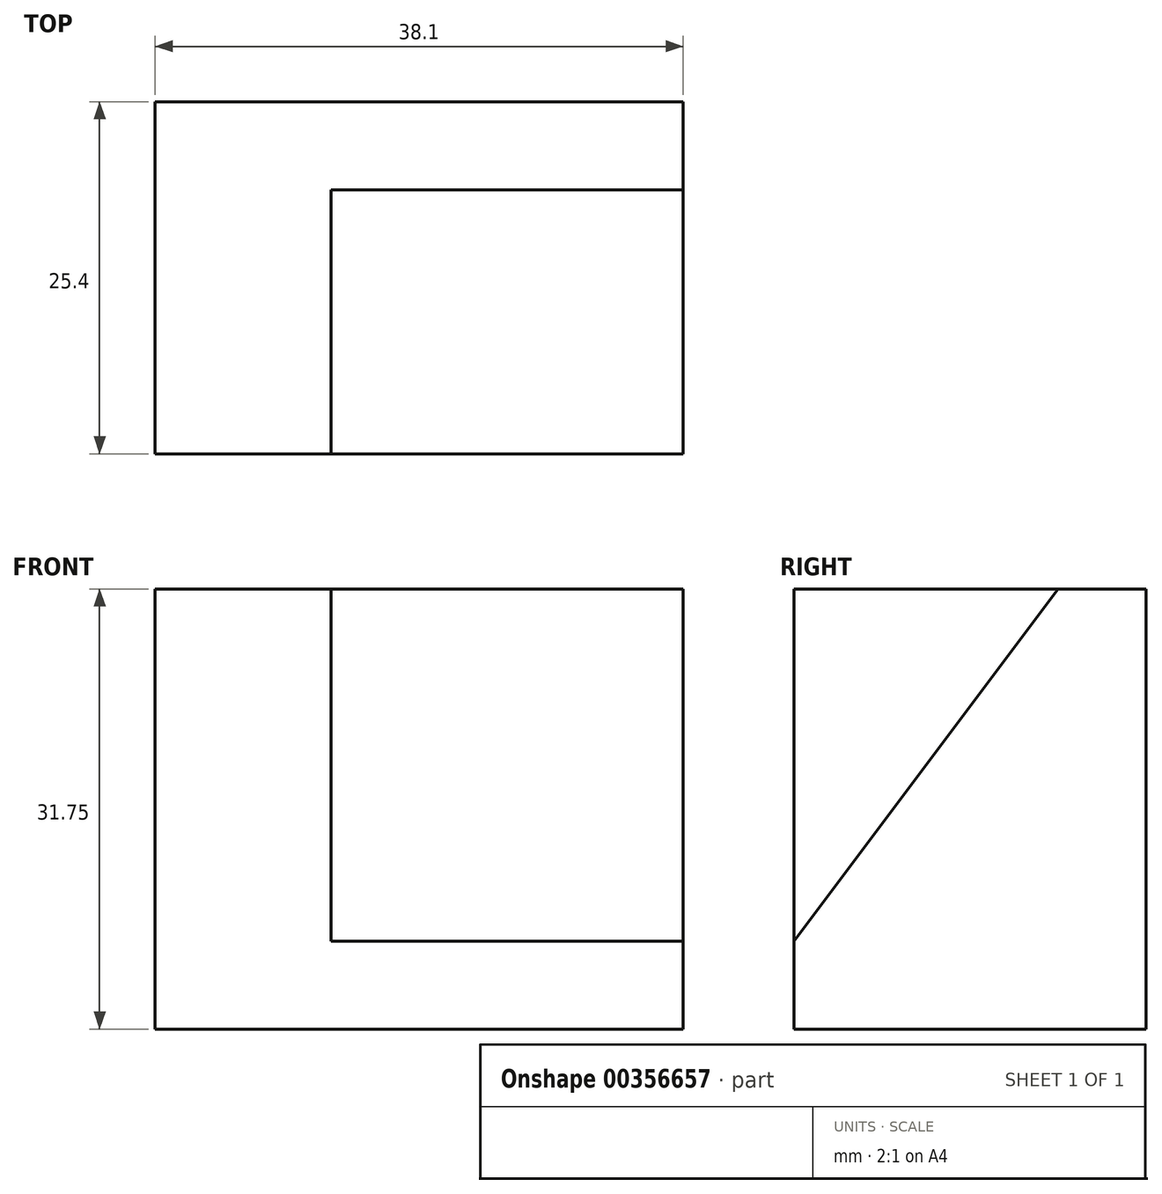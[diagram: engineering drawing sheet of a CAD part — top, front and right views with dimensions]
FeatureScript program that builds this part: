
annotation { "Feature Type Name" : "Feature", "Feature Type Description" : "" }
export const myFeature = defineFeature(function(context is Context, id is Id, definition is map)
    precondition{}
    {
        {
            var Q0;
            Q0=qCreatedBy(makeId("Front.planeOp"),FACE);
            var sketch = newSketch(context, id + "F0", { "sketchPlane" : qUnion([Q0])});
            skLineSegment(sketch, "E0", {"start": v(-35.9, 29.87) * mm, "end": v(-35.9, -1.88) * mm});
            skLineSegment(sketch, "E1", {"start": v(-35.9, -1.88) * mm, "end": v(2.2, -1.88) * mm});
            skLineSegment(sketch, "E2", {"start": v(2.2, -1.88) * mm, "end": v(2.2, 29.87) * mm});
            skLineSegment(sketch, "E3", {"start": v(2.2, 29.87) * mm, "end": v(-35.9, 29.87) * mm});
            skSolve(sketch);
        }
        {
            var Q0;
            Q0=makeQuery(id+"F0.imprint","IMPRINT",FACE,{"disambiguationData":[TD([[makeQuery(id+"F0.imprint","IMPRINT",EDGE,{"derivedFrom":sQuery(id+"F0.wireOp",EDGE,"E0")}),1.0]])]});
            extrude(context, id + "F1", {"entities" : qUnion([Q0]), "depth" : 25.4 * mm});
        }
        {
            var Q0;
            Q0=makeQuery(id+"F1.opExtrude","SWEPT_FACE",FACE,{"disambiguationData":[OSD([sQuery(id+"F0.wireOp",EDGE,"E3")])]});
            var sketch = newSketch(context, id + "F2", { "sketchPlane" : qUnion([Q0])});
            skLineSegment(sketch, "E4", {"start": v(2.2, -6.35) * mm, "end": v(-23.2, -6.35) * mm});
            skLineSegment(sketch, "E5", {"start": v(-23.2, -6.35) * mm, "end": v(-23.2, -25.4) * mm});
            skSolve(sketch);
        }
        {
            var Q0;
            {var subQ0=sQuery(id+"F2.wireOp",EDGE,"E4");Q0=makeQuery(id+"F2.imprint","IMPRINT",FACE,{"disambiguationData":[TD([[makeQuery(id+"F2.imprint","IMPRINT",EDGE,{"derivedFrom":subQ0}),1.0]])]});}
            extrude(context, id + "F3", {"entities" : qUnion([Q0]), "operationType" : NewBodyOperationType.ADD, "depth" : 25.4 * mm});
        }
        {
            var Q0;
            Q0=makeQuery(id+"F3.opExtrude","CAP_FACE",FACE,{"disambiguationData":[OSD([sQuery(id+"F0.wireOp",EDGE,"E2"),sQuery(id+"F0.wireOp",EDGE,"E3"),sQuery(id+"F2.wireOp",EDGE,"E4"),sQuery(id+"F2.wireOp",EDGE,"E5")])],"isStart":false});
            extrude(context, id + "F4", {"entities" : qUnion([Q0]), "operationType" : NewBodyOperationType.REMOVE, "oppositeDirection" : true, "depth" : 25.4 * mm});
        }
        {
            var Q0;
            {var subQ0=sQuery(id+"F0.wireOp",EDGE,"E2");Q0=makeQuery(id+"F3.boolean.opBoolean","MERGE",FACE,{"derivedFrom":[makeQuery(id+"F1.opExtrude","SWEPT_FACE",FACE,{"disambiguationData":[OSD([subQ0])]}),makeQuery(id+"F3.opExtrude","SWEPT_FACE",FACE,{"disambiguationData":[OSD([subQ0,sQuery(id+"F0.wireOp",EDGE,"E3")])]})]});}
            var sketch = newSketch(context, id + "F5", { "sketchPlane" : qUnion([Q0])});
            skLineSegment(sketch, "E6", {"start": v(-6.35, 29.87) * mm, "end": v(-25.4, 4.47) * mm});
            skLineSegment(sketch, "E7", {"start": v(-25.4, 4.47) * mm, "end": v(-25.4, 29.87) * mm});
            skLineSegment(sketch, "E8", {"start": v(-25.4, 29.87) * mm, "end": v(-6.35, 29.87) * mm});
            skSolve(sketch);
        }
        {
            var Q0;
            Q0=makeQuery(id+"F5.imprint","IMPRINT",FACE,{"disambiguationData":[TD([[makeQuery(id+"F5.imprint","IMPRINT",EDGE,{"derivedFrom":sQuery(id+"F5.wireOp",EDGE,"E6")}),-1.0]])]});
            extrude(context, id + "F6", {"entities" : qUnion([Q0]), "operationType" : NewBodyOperationType.REMOVE, "oppositeDirection" : true, "depth" : 25.4 * mm});
        }
    });
